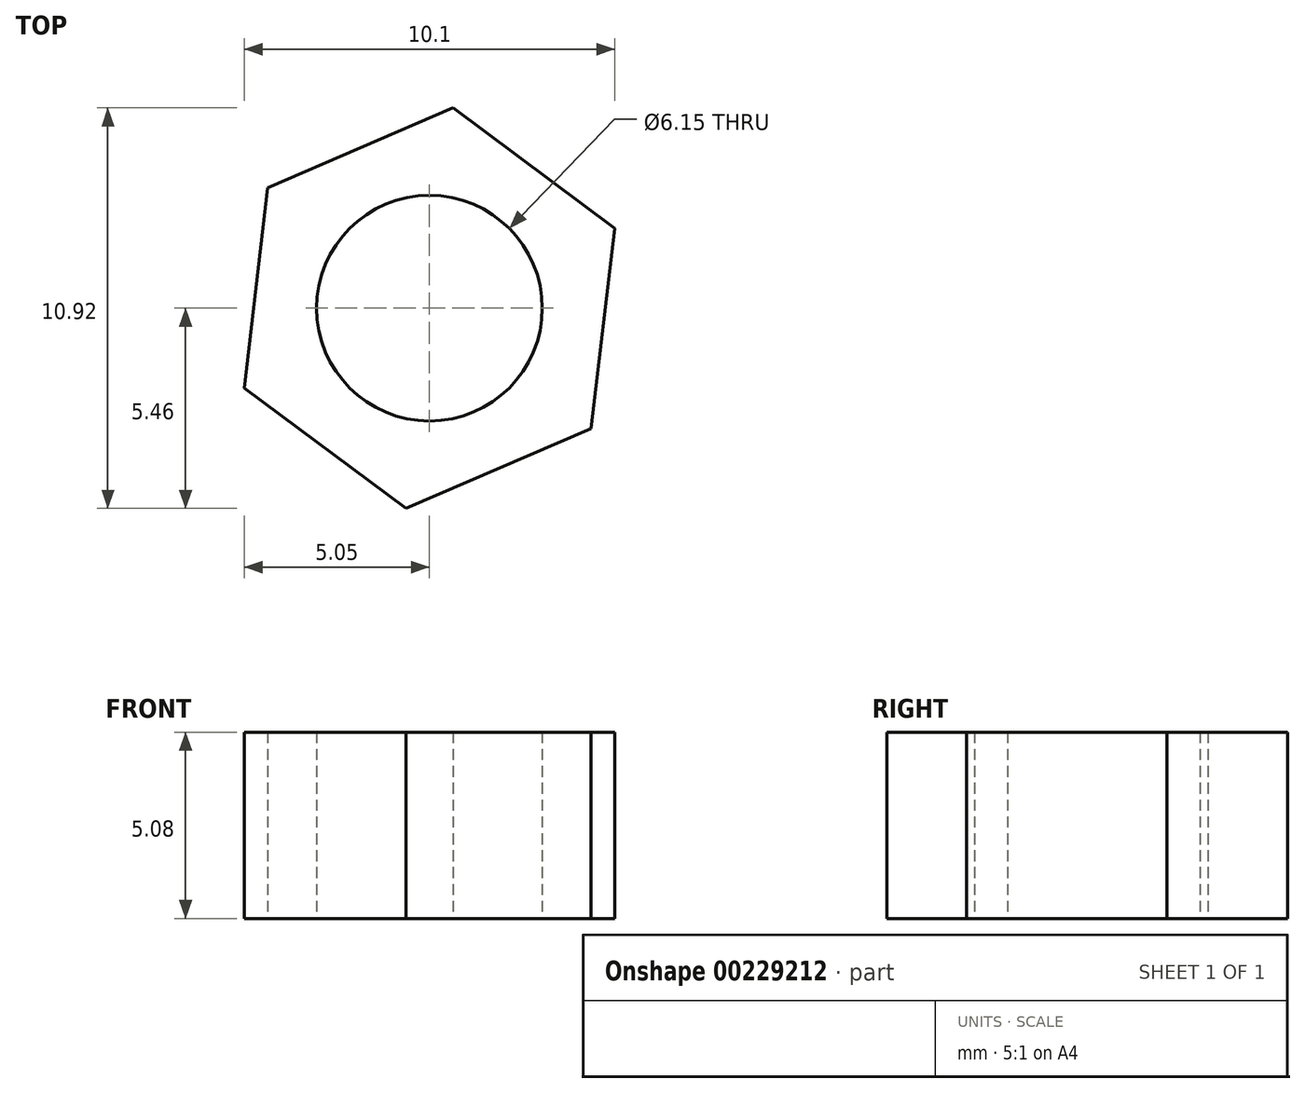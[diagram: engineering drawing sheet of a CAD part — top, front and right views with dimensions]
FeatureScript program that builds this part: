
annotation { "Feature Type Name" : "Feature", "Feature Type Description" : "" }
export const myFeature = defineFeature(function(context is Context, id is Id, definition is map)
    precondition{}
    {
        {
            var Q0;
            Q0=qCreatedBy(makeId("Top.planeOp"),FACE);
            var sketch = newSketch(context, id + "F0", { "sketchPlane" : qUnion([Q0])});
            skCircle(sketch, "E0", {"center": v(0, 0) * mm, "radius": 3.08 * mm});
            skCircle(sketch, "E1.cCircle", {"center": v(0, 0) * mm, "radius": 4.76 * mm, "construction": true});
            skLineSegment(sketch, "E1.0", {"start": v(4.4, -3.29) * mm, "end": v(-0.64, -5.46) * mm});
            skLineSegment(sketch, "E1.1", {"start": v(-0.64, -5.46) * mm, "end": v(-5.05, -2.17) * mm});
            skLineSegment(sketch, "E1.2", {"start": v(-5.05, -2.17) * mm, "end": v(-4.4, 3.29) * mm});
            skLineSegment(sketch, "E1.3", {"start": v(-4.4, 3.29) * mm, "end": v(0.64, 5.46) * mm});
            skLineSegment(sketch, "E1.4", {"start": v(0.64, 5.46) * mm, "end": v(5.05, 2.17) * mm});
            skLineSegment(sketch, "E1.5", {"start": v(5.05, 2.17) * mm, "end": v(4.4, -3.29) * mm});
            skPoint(sketch, "E1.0.midPoint", {"position": v(1.88, -4.37) * mm});
            skSolve(sketch);
        }
        {
            var Q0;
            Q0 = qSketchRegion(id + "F0", true);
            extrude(context, id + "F1", {"entities" : qUnion([Q0]), "depth" : 5.08 * mm});
        }
    });
